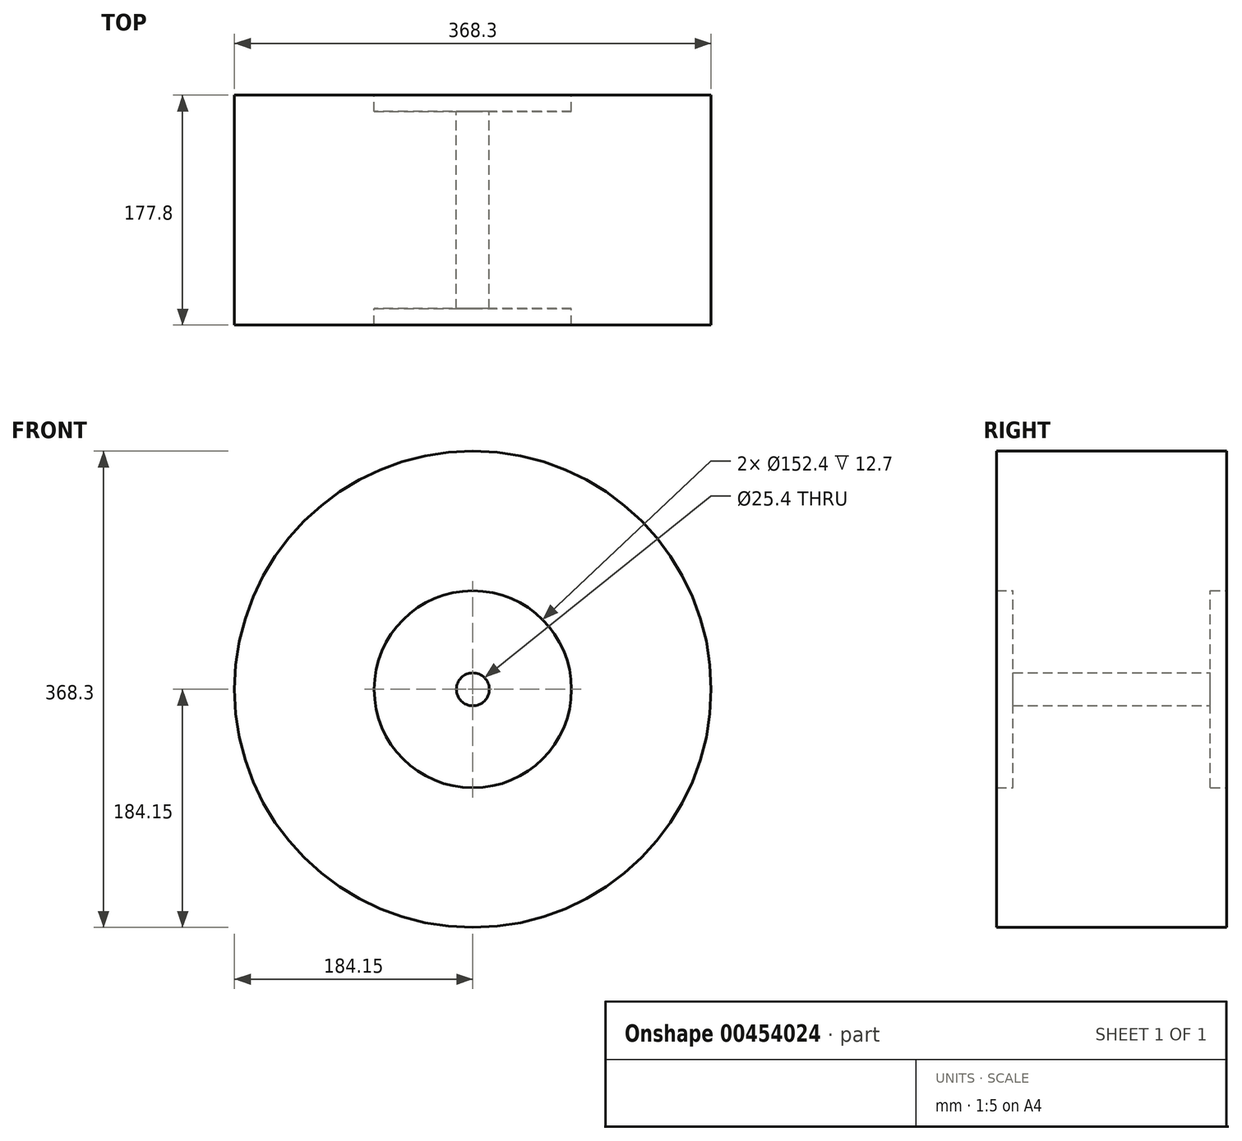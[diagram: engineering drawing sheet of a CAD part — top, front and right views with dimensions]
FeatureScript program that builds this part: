
annotation { "Feature Type Name" : "Feature", "Feature Type Description" : "" }
export const myFeature = defineFeature(function(context is Context, id is Id, definition is map)
    precondition{}
    {
        {
            var Q0;
            Q0=qCreatedBy(makeId("Front.planeOp"),FACE);
            var sketch = newSketch(context, id + "F0", { "sketchPlane" : qUnion([Q0])});
            skCircle(sketch, "E0", {"center": v(0, 0) * mm, "radius": 184.15 * mm});
            skCircle(sketch, "E1", {"center": v(0, 0) * mm, "radius": 76.2 * mm});
            skSolve(sketch);
        }
        {
            var Q0;
            Q0=makeQuery(id+"F0.imprint","IMPRINT",FACE,{"disambiguationData":[TD([[makeQuery(id+"F0.imprint","IMPRINT",EDGE,{"derivedFrom":sQuery(id+"F0.wireOp",EDGE,"E0")}),1.0]])]});
            extrude(context, id + "F1", {"entities" : qUnion([Q0]), "endBound" : BoundingType.SYMMETRIC, "depth" : 177.8 * mm});
        }
        {
            var Q0;
            Q0=qCreatedBy(makeId("Front.planeOp"),FACE);
            var sketch = newSketch(context, id + "F2", { "sketchPlane" : qUnion([Q0])});
            skCircle(sketch, "E2", {"center": v(0, 0) * mm, "radius": 76.2 * mm});
            skSolve(sketch);
        }
        {
            var Q0;
            Q0=makeQuery(id+"F2.imprint","IMPRINT",FACE,{"disambiguationData":[TD([[makeQuery(id+"F2.imprint","IMPRINT",EDGE,{"derivedFrom":sQuery(id+"F2.wireOp",EDGE,"E2")}),1.0]])]});
            extrude(context, id + "F3", {"entities" : qUnion([Q0]), "operationType" : NewBodyOperationType.ADD, "endBound" : BoundingType.SYMMETRIC, "depth" : 152.4 * mm});
        }
        {
            var Q0;
            Q0=makeQuery(id+"F3.opExtrude","CAP_FACE",FACE,{"disambiguationData":[OSD([sQuery(id+"F2.wireOp",EDGE,"E2")])],"isStart":false});
            var sketch = newSketch(context, id + "F4", { "sketchPlane" : qUnion([Q0])});
            skCircle(sketch, "E3", {"center": v(0, 0) * mm, "radius": 12.7 * mm});
            skSolve(sketch);
        }
        {
            var Q0;
            Q0=makeQuery(id+"F4.imprint","IMPRINT",FACE,{"disambiguationData":[TD([[makeQuery(id+"F4.imprint","IMPRINT",EDGE,{"derivedFrom":sQuery(id+"F4.wireOp",EDGE,"E3")}),1.0]])]});
            extrude(context, id + "F5", {"entities" : qUnion([Q0]), "operationType" : NewBodyOperationType.REMOVE, "endBound" : BoundingType.SYMMETRIC, "depth" : 152.4 * mm});
        }
        {
            var Q0;
            Q0=makeQuery(id+"F5.boolean.opBoolean","COPY",FACE,{"derivedFrom":makeQuery(id+"F5.opExtrude","CAP_FACE",FACE,{"disambiguationData":[OSD([sQuery(id+"F4.wireOp",EDGE,"E3")])],"isStart":true})});
            var sketch = newSketch(context, id + "F6", { "sketchPlane" : qUnion([Q0])});
            skSolve(sketch);
        }
        {
            var Q0;
            Q0=makeQuery(id+"F6.imprint","IMPRINT",FACE,{"disambiguationData":[TD([[makeQuery(id+"F6.imprint","IMPRINT",EDGE,{"derivedFrom":makeQuery(id+"F5.boolean.opBoolean","COPY",EDGE,{"derivedFrom":makeQuery(id+"F5.opExtrude","CAP_EDGE",EDGE,{"disambiguationData":[OSD([sQuery(id+"F4.wireOp",EDGE,"E3")])],"isStart":true})})}),1.0]])]});
            extrude(context, id + "F7", {"entities" : qUnion([Q0]), "operationType" : NewBodyOperationType.REMOVE, "endBound" : BoundingType.SYMMETRIC, "depth" : 152.4 * mm});
        }
    });
